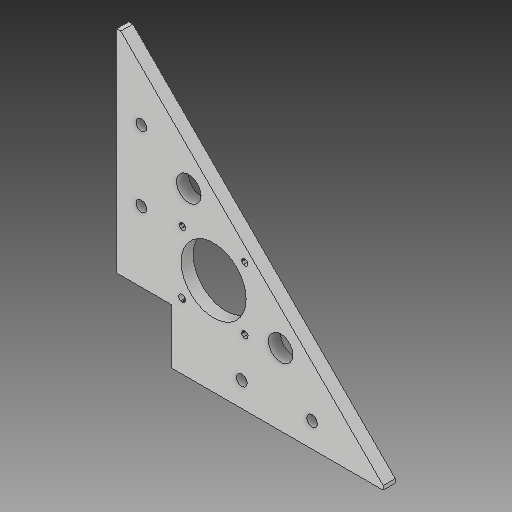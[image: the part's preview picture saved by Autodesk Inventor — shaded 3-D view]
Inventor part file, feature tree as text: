
AUTODESK INVENTOR PART (.ipt)
format: ipt  version: 2018 (Build 220112000, 112)  size: 425,472 bytes
history: native  units: mm
features: extrude x2, sketch x2
ambient origin geometry x8: Origin, YZ Plane, XZ Plane, XY Plane, X Axis, Y Axis, Z Axis, Center Point
bodies: Solid1 (feature_tree)
feature tree (4):
  extrude  "Extrusion1"  Depth=6.0mm
  extrude  "Extrusion3"  Depth=6.0mm
  sketch  "Sketch1"  dims[d0=6.0mm d1=0.0mm d2=5.3mm]
  sketch  "Sketch2"  dims[d3=5.3mm d4=5.3mm d5=5.3mm d6=3.2mm d7=3.2mm d8=3.2mm d9=3.2mm d10=12.2mm d11=12.2mm d12=32.2mm d15=6.0mm d16=0.0mm]
